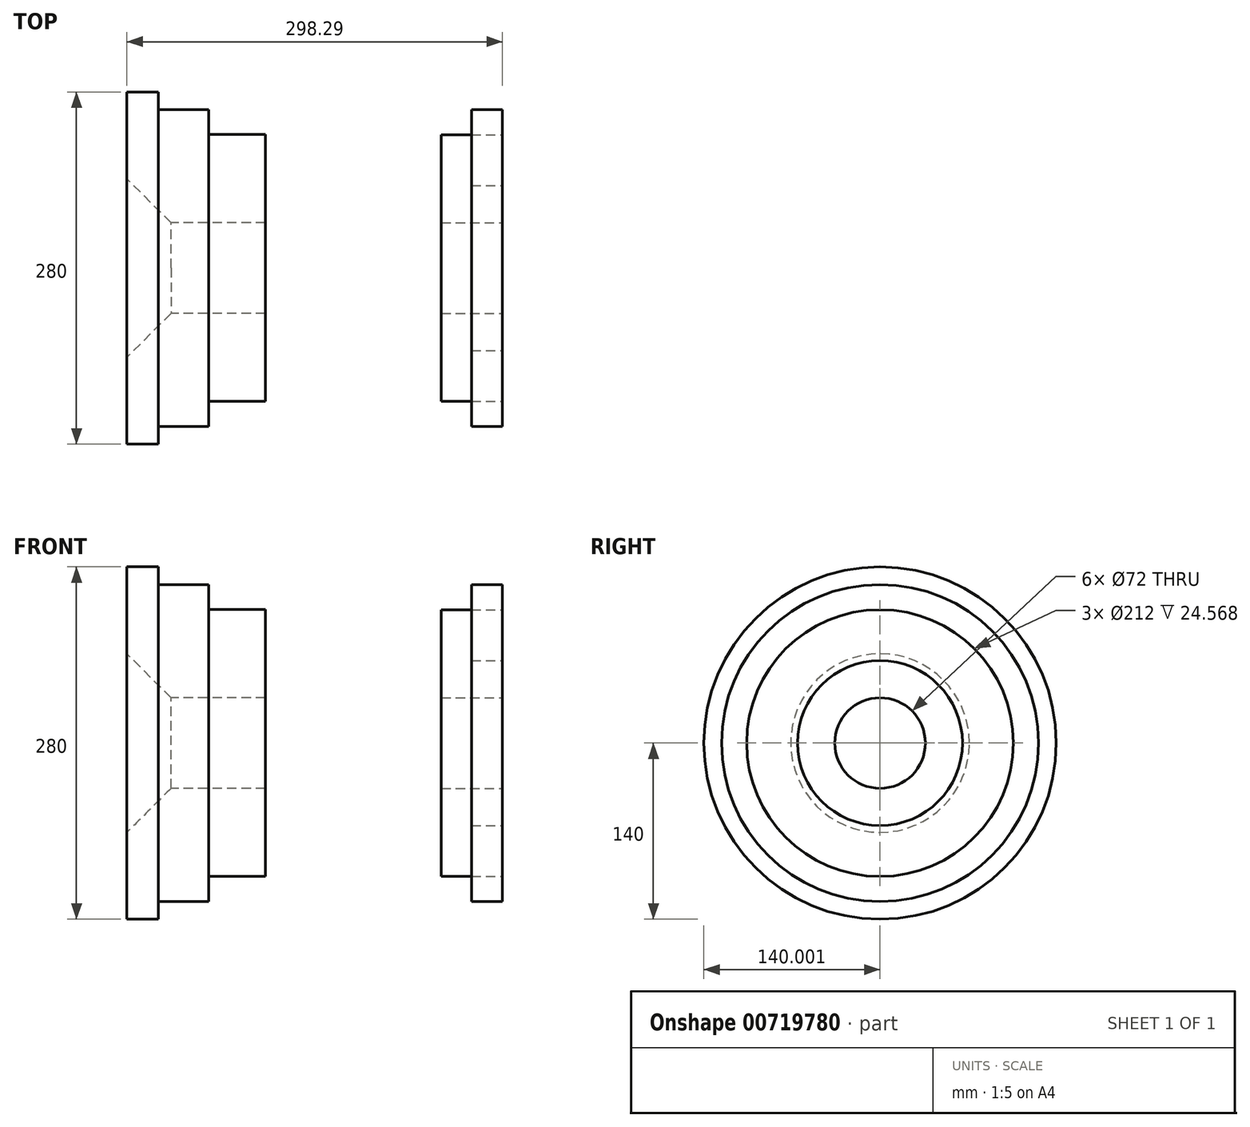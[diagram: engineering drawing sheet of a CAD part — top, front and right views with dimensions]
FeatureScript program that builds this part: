
annotation { "Feature Type Name" : "Feature", "Feature Type Description" : "" }
export const myFeature = defineFeature(function(context is Context, id is Id, definition is map)
    precondition{}
    {
        {
            var Q0;
            Q0=qCreatedBy(makeId("Top.planeOp"),FACE);
            var sketch = newSketch(context, id + "F0", { "sketchPlane" : qUnion([Q0])});
            skLineSegment(sketch, "E0", {"start": v(-637.4, 22.98) * mm, "end": v(491.23, 22.98) * mm});
            skLineSegment(sketch, "E1.bottom", {"start": v(-53.76, 58.98) * mm, "end": v(56.24, 58.98) * mm});
            skLineSegment(sketch, "E1.top", {"start": v(-53.76, 162.98) * mm, "end": v(56.24, 162.98) * mm});
            skLineSegment(sketch, "E1.left", {"start": v(-53.76, 162.98) * mm, "end": v(-53.76, 58.98) * mm});
            skLineSegment(sketch, "E1.right", {"start": v(56.24, 162.98) * mm, "end": v(56.24, 58.98) * mm});
            skLineSegment(sketch, "E2.left", {"start": v(56.24, 162.98) * mm, "end": v(56.24, 148.98) * mm});
            skLineSegment(sketch, "E3.left", {"start": v(56.24, 148.98) * mm, "end": v(56.24, 109.08) * mm});
            skLineSegment(sketch, "E4.bottom", {"start": v(56.24, 162.98) * mm, "end": v(-28.76, 162.98) * mm});
            skLineSegment(sketch, "E4.top", {"start": v(56.24, 148.98) * mm, "end": v(-28.76, 148.98) * mm});
            skLineSegment(sketch, "E4.right", {"start": v(-28.76, 162.98) * mm, "end": v(-28.76, 148.98) * mm});
            skPoint(sketch, "E5.oppositeSnap0", {"position": v(56.24, 129.03) * mm});
            skLineSegment(sketch, "E5.bottom", {"start": v(56.24, 148.98) * mm, "end": v(11.24, 148.98) * mm});
            skLineSegment(sketch, "E5.top", {"start": v(56.24, 129.03) * mm, "end": v(11.24, 129.03) * mm});
            skLineSegment(sketch, "E5.left", {"start": v(56.24, 148.98) * mm, "end": v(56.24, 129.03) * mm});
            skLineSegment(sketch, "E5.right", {"start": v(11.24, 148.98) * mm, "end": v(11.24, 129.03) * mm});
            skLineSegment(sketch, "E6.bottom", {"start": v(196, 58.98) * mm, "end": v(244.53, 58.98) * mm});
            skLineSegment(sketch, "E6.top", {"start": v(196, 128.98) * mm, "end": v(244.53, 128.98) * mm});
            skLineSegment(sketch, "E6.left", {"start": v(196, 58.98) * mm, "end": v(196, 128.98) * mm});
            skLineSegment(sketch, "E6.right", {"start": v(244.53, 58.98) * mm, "end": v(244.53, 128.98) * mm});
            skLineSegment(sketch, "E7.bottom", {"start": v(244.53, 148.98) * mm, "end": v(151, 148.98) * mm});
            skLineSegment(sketch, "E7.top", {"start": v(244.53, 128.98) * mm, "end": v(151, 128.98) * mm});
            skLineSegment(sketch, "E7.left", {"start": v(244.53, 148.98) * mm, "end": v(244.53, 128.98) * mm});
            skLineSegment(sketch, "E7.right", {"start": v(151, 148.98) * mm, "end": v(151, 128.98) * mm});
            skLineSegment(sketch, "E8.bottom", {"start": v(244.53, 58.98) * mm, "end": v(220, 58.98) * mm});
            skLineSegment(sketch, "E8.left", {"start": v(244.53, 58.98) * mm, "end": v(244.53, 88.48) * mm});
            skLineSegment(sketch, "E9.bottom", {"start": v(244.53, 128.98) * mm, "end": v(219.97, 128.98) * mm});
            skLineSegment(sketch, "E9.left", {"start": v(244.53, 128.98) * mm, "end": v(244.53, 90.07) * mm});
            skLineSegment(sketch, "E10.top", {"start": v(219.97, 148.98) * mm, "end": v(219.97, 148.98) * mm});
            skLineSegment(sketch, "E11.bottom", {"start": v(244.53, 88.48) * mm, "end": v(219.97, 88.48) * mm});
            skLineSegment(sketch, "E11.top", {"start": v(244.53, 148.98) * mm, "end": v(219.97, 148.98) * mm});
            skLineSegment(sketch, "E11.left", {"start": v(244.53, 88.48) * mm, "end": v(244.53, 148.98) * mm});
            skLineSegment(sketch, "E11.right", {"start": v(219.97, 88.48) * mm, "end": v(219.97, 148.98) * mm});
            skLineSegment(sketch, "E12", {"start": v(-630.84, -15.11) * mm, "end": v(497.76, -15.11) * mm});
            skSolve(sketch);
        }
        {
            var Q0;
            Q0=makeQuery(id+"F0.imprint","IMPRINT",FACE,{"disambiguationData":[TD([[makeQuery(id+"F0.imprint","IMPRINT",EDGE,{"derivedFrom":sQuery(id+"F0.wireOp",EDGE,"E1.bottom")}),1.0]])]});
            var Q1;
            Q1=sQuery(id+"F0.wireOp",EDGE,"E0");
            revolve(context, id + "F1", {"surfaceOperationType" : NewSurfaceOperationType.NEW, "entities" : qUnion([Q0]), "axis" : qUnion([Q1]), "revolveType" : RevolveType.FULL});
        }
        {
            var Q0;
            Q0=makeQuery(id+"F0.imprint","IMPRINT",FACE,{"disambiguationData":[TD([[makeQuery(id+"F0.imprint","IMPRINT",EDGE,{"derivedFrom":sQuery(id+"F0.wireOp",EDGE,"E6.bottom")}),1.0]])]});
            var Q1;
            Q1=makeQuery(id+"F0.imprint","IMPRINT",FACE,{"disambiguationData":[TD([[makeQuery(id+"F0.imprint","IMPRINT",EDGE,{"derivedFrom":sQuery(id+"F0.wireOp",EDGE,"E7.bottom")}),1.0]])]});
            var Q2;
            Q2=makeQuery(id+"F1.opRevolve","SWEPT_EDGE",EDGE,{"disambiguationData":[OSD([sQuery(id+"F0.wireOp",EDGE,"E1.bottom"),sQuery(id+"F0.wireOp",EDGE,"E1.right")])]});
            revolve(context, id + "F2", {"surfaceOperationType" : NewSurfaceOperationType.NEW, "entities" : qUnion([Q0, Q1]), "axis" : qUnion([Q2]), "revolveType" : RevolveType.FULL});
        }
        {
            var Q0;
            Q0=makeQuery(id+"F1.opRevolve","SWEPT_EDGE",EDGE,{"disambiguationData":[OSD([sQuery(id+"F0.wireOp",EDGE,"E1.bottom"),sQuery(id+"F0.wireOp",EDGE,"E1.left")])]});
            chamfer(context, id + "F3", {"entities" : qUnion([Q0]), "width" : 35 * mm, "tangentPropagation" : true});
        }
    });
